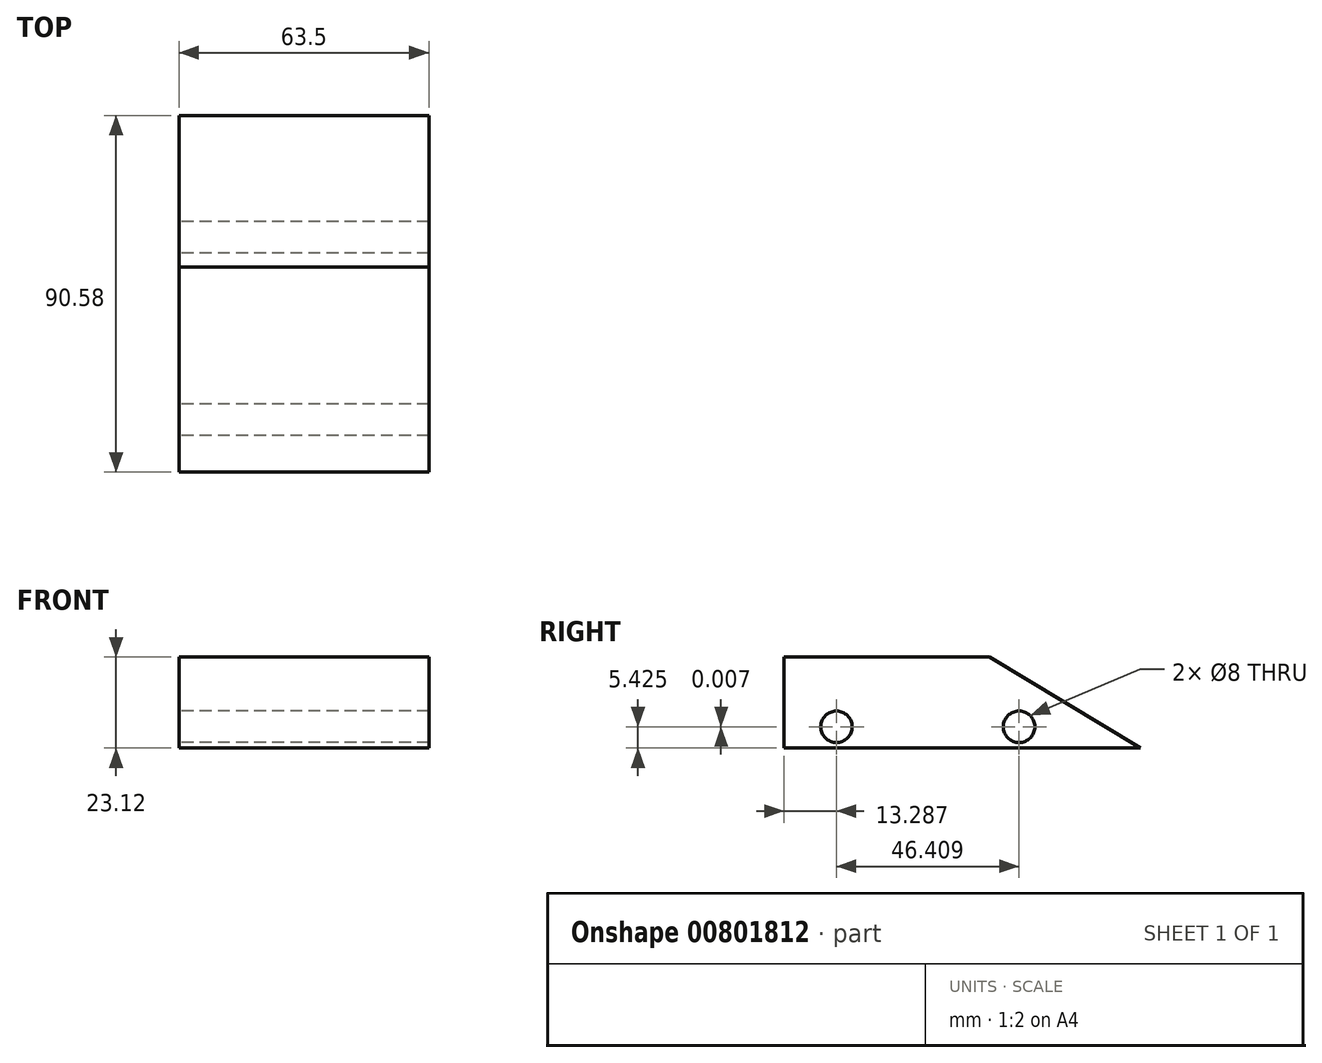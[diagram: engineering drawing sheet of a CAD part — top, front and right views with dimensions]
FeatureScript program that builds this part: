
annotation { "Feature Type Name" : "Feature", "Feature Type Description" : "" }
export const myFeature = defineFeature(function(context is Context, id is Id, definition is map)
    precondition{}
    {
        {
            var Q0;
            Q0=qCreatedBy(makeId("Right.planeOp"),FACE);
            var sketch = newSketch(context, id + "F0", { "sketchPlane" : qUnion([Q0])});
            skLineSegment(sketch, "E0", {"start": v(-52.16, 11.09) * mm, "end": v(-52.16, -12.03) * mm});
            skLineSegment(sketch, "E1", {"start": v(-52.16, -12.03) * mm, "end": v(38.42, -12.03) * mm});
            skLineSegment(sketch, "E2", {"start": v(-52.16, 11.09) * mm, "end": v(0, 11.09) * mm});
            skLineSegment(sketch, "E3", {"start": v(0, 11.09) * mm, "end": v(38.42, -12.03) * mm});
            skCircle(sketch, "E4", {"center": v(-38.87, -6.6) * mm, "radius": 4 * mm});
            skCircle(sketch, "E5", {"center": v(7.54, -6.6) * mm, "radius": 4 * mm});
            skSolve(sketch);
        }
        {
            var Q0;
            Q0 = qSketchRegion(id + "F0", true);
            extrude(context, id + "F1", {"entities" : qUnion([Q0]), "depth" : 63.5 * mm, "offsetDistance" : 25.4 * mm});
        }
    });
